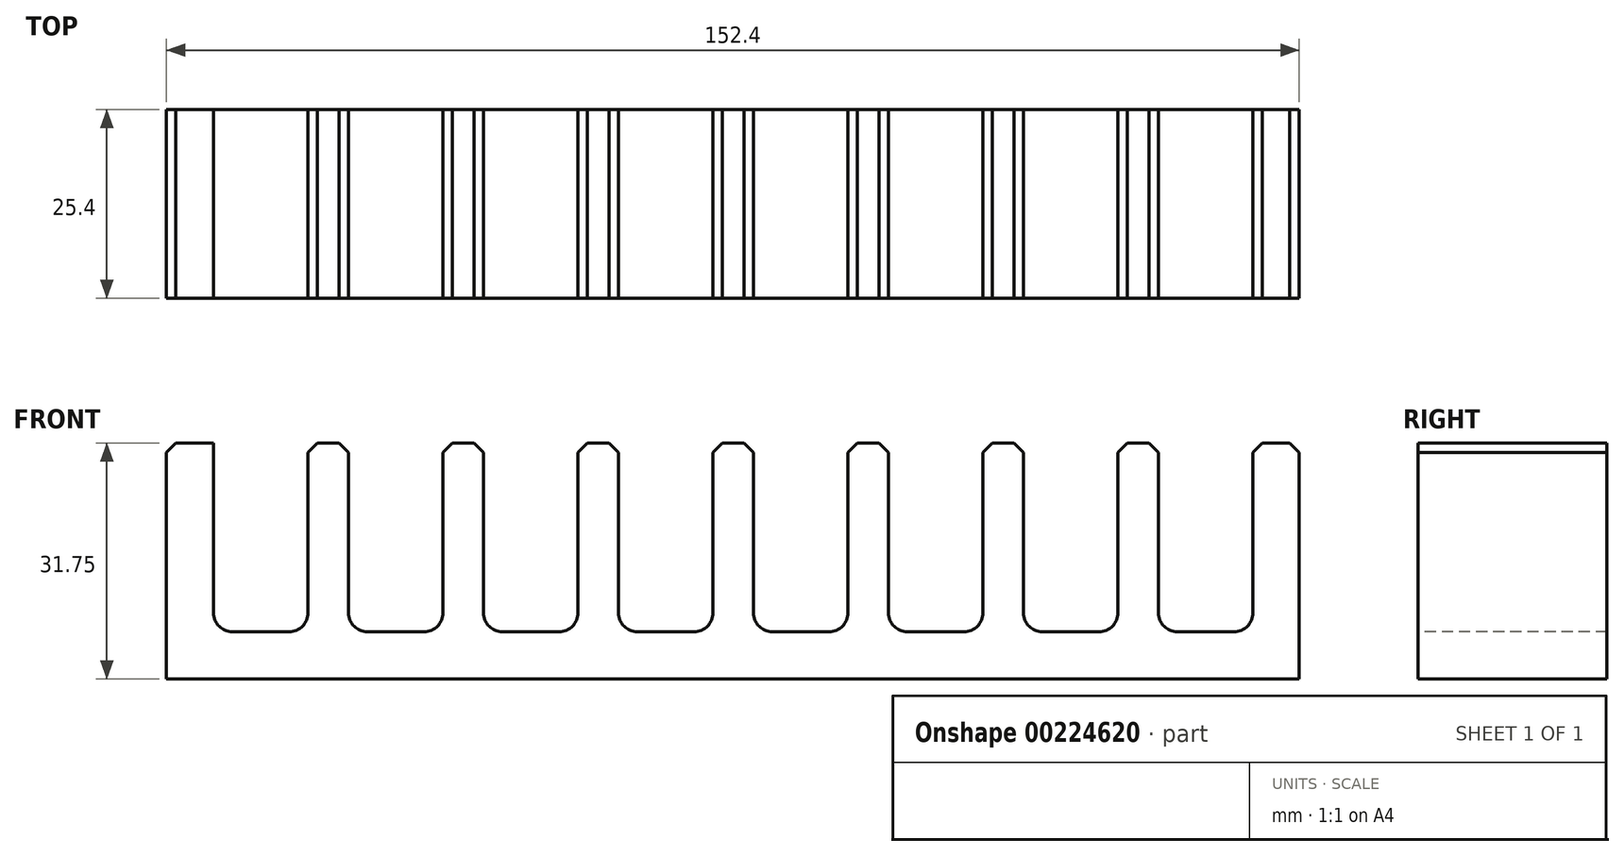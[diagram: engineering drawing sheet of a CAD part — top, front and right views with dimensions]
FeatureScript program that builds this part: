
annotation { "Feature Type Name" : "Feature", "Feature Type Description" : "" }
export const myFeature = defineFeature(function(context is Context, id is Id, definition is map)
    precondition{}
    {
        {
            var Q0;
            Q0=qCreatedBy(makeId("Top.planeOp"),FACE);
            var sketch = newSketch(context, id + "F0", { "sketchPlane" : qUnion([Q0])});
            skLineSegment(sketch, "E0.bottom", {"start": v(76.2, -12.7) * mm, "end": v(-76.2, -12.7) * mm});
            skLineSegment(sketch, "E0.top", {"start": v(76.2, 12.7) * mm, "end": v(-76.2, 12.7) * mm});
            skLineSegment(sketch, "E0.left", {"start": v(76.2, -12.7) * mm, "end": v(76.2, 12.7) * mm});
            skLineSegment(sketch, "E0.right", {"start": v(-76.2, -12.7) * mm, "end": v(-76.2, 12.7) * mm});
            skPoint(sketch, "E0.middle", {"position": v(0, 0) * mm});
            skSolve(sketch);
        }
        {
            var Q0;
            Q0 = qSketchRegion(id + "F0", true);
            extrude(context, id + "F1", {"entities" : qUnion([Q0]), "depth" : 31.75 * mm});
        }
        {
            var Q0;
            Q0=makeQuery(id+"F1.opExtrude","SWEPT_FACE",FACE,{"disambiguationData":[OSD([sQuery(id+"F0.wireOp",EDGE,"E0.bottom")])]});
            var sketch = newSketch(context, id + "F2", { "sketchPlane" : qUnion([Q0])});
            skLineSegment(sketch, "E1.bottom", {"start": v(-69.85, 31.75) * mm, "end": v(-57.15, 31.75) * mm});
            skLineSegment(sketch, "E1.top", {"start": v(-69.85, 6.35) * mm, "end": v(-57.15, 6.35) * mm});
            skLineSegment(sketch, "E1.left", {"start": v(-69.85, 31.75) * mm, "end": v(-69.85, 6.35) * mm});
            skLineSegment(sketch, "E1.right", {"start": v(-57.15, 31.75) * mm, "end": v(-57.15, 6.35) * mm});
            skLineSegment(sketch, "E2.1.0.0", {"start": v(-51.69, 31.75) * mm, "end": v(-38.99, 31.75) * mm});
            skLineSegment(sketch, "E2.1.0.1", {"start": v(-51.69, 6.35) * mm, "end": v(-38.99, 6.35) * mm});
            skLineSegment(sketch, "E2.1.0.2", {"start": v(-51.69, 31.75) * mm, "end": v(-51.69, 6.35) * mm});
            skLineSegment(sketch, "E2.1.0.3", {"start": v(-38.99, 31.75) * mm, "end": v(-38.99, 6.35) * mm});
            skLineSegment(sketch, "E2.2.0.0", {"start": v(-33.53, 31.75) * mm, "end": v(-20.83, 31.75) * mm});
            skLineSegment(sketch, "E2.2.0.1", {"start": v(-33.53, 6.35) * mm, "end": v(-20.83, 6.35) * mm});
            skLineSegment(sketch, "E2.2.0.2", {"start": v(-33.53, 31.75) * mm, "end": v(-33.53, 6.35) * mm});
            skLineSegment(sketch, "E2.2.0.3", {"start": v(-20.83, 31.75) * mm, "end": v(-20.83, 6.35) * mm});
            skLineSegment(sketch, "E2.3.0.0", {"start": v(-15.37, 31.75) * mm, "end": v(-2.67, 31.75) * mm});
            skLineSegment(sketch, "E2.3.0.1", {"start": v(-15.37, 6.35) * mm, "end": v(-2.67, 6.35) * mm});
            skLineSegment(sketch, "E2.3.0.2", {"start": v(-15.37, 31.75) * mm, "end": v(-15.37, 6.35) * mm});
            skLineSegment(sketch, "E2.3.0.3", {"start": v(-2.67, 31.75) * mm, "end": v(-2.67, 6.35) * mm});
            skLineSegment(sketch, "E2.4.0.0", {"start": v(2.8, 31.75) * mm, "end": v(15.5, 31.75) * mm});
            skLineSegment(sketch, "E2.4.0.1", {"start": v(2.8, 6.35) * mm, "end": v(15.5, 6.35) * mm});
            skLineSegment(sketch, "E2.4.0.2", {"start": v(2.8, 31.75) * mm, "end": v(2.8, 6.35) * mm});
            skLineSegment(sketch, "E2.4.0.3", {"start": v(15.5, 31.75) * mm, "end": v(15.5, 6.35) * mm});
            skLineSegment(sketch, "E2.5.0.0", {"start": v(20.95, 31.75) * mm, "end": v(33.65, 31.75) * mm});
            skLineSegment(sketch, "E2.5.0.1", {"start": v(20.95, 6.35) * mm, "end": v(33.65, 6.35) * mm});
            skLineSegment(sketch, "E2.5.0.2", {"start": v(20.95, 31.75) * mm, "end": v(20.95, 6.35) * mm});
            skLineSegment(sketch, "E2.5.0.3", {"start": v(33.65, 31.75) * mm, "end": v(33.65, 6.35) * mm});
            skLineSegment(sketch, "E2.6.0.0", {"start": v(39.12, 31.75) * mm, "end": v(51.82, 31.75) * mm});
            skLineSegment(sketch, "E2.6.0.1", {"start": v(39.12, 6.35) * mm, "end": v(51.82, 6.35) * mm});
            skLineSegment(sketch, "E2.6.0.2", {"start": v(39.12, 31.75) * mm, "end": v(39.12, 6.35) * mm});
            skLineSegment(sketch, "E2.6.0.3", {"start": v(51.82, 31.75) * mm, "end": v(51.82, 6.35) * mm});
            skLineSegment(sketch, "E2.7.0.0", {"start": v(57.28, 31.75) * mm, "end": v(69.98, 31.75) * mm});
            skLineSegment(sketch, "E2.7.0.1", {"start": v(57.28, 6.35) * mm, "end": v(69.98, 6.35) * mm});
            skLineSegment(sketch, "E2.7.0.2", {"start": v(57.28, 31.75) * mm, "end": v(57.28, 6.35) * mm});
            skLineSegment(sketch, "E2.7.0.3", {"start": v(69.98, 31.75) * mm, "end": v(69.98, 6.35) * mm});
            skLineSegment(sketch, "E2.direction1", {"start": v(-69.85, 6.35) * mm, "end": v(-51.69, 6.35) * mm, "construction": true});
            skSolve(sketch);
        }
        {
            var Q0;
            Q0 = qSketchRegion(id + "F2", true);
            extrude(context, id + "F3", {"entities" : qUnion([Q0]), "operationType" : NewBodyOperationType.REMOVE, "endBound" : BoundingType.THROUGH_ALL, "oppositeDirection" : true, "depth" : 25.4 * mm});
        }
        {
            var Q0;
            Q0=makeQuery(id+"F3.boolean.opBoolean","COPY",EDGE,{"derivedFrom":makeQuery(id+"F3.opExtrude","SWEPT_EDGE",EDGE,{"disambiguationData":[OSD([sQuery(id+"F2.wireOp",EDGE,"E1.top"),sQuery(id+"F2.wireOp",EDGE,"E1.left")])]})});
            var Q1;
            Q1=makeQuery(id+"F3.boolean.opBoolean","COPY",EDGE,{"derivedFrom":makeQuery(id+"F3.opExtrude","SWEPT_EDGE",EDGE,{"disambiguationData":[OSD([sQuery(id+"F2.wireOp",EDGE,"E1.top"),sQuery(id+"F2.wireOp",EDGE,"E1.right")])]})});
            var Q2;
            Q2=makeQuery(id+"F3.boolean.opBoolean","COPY",EDGE,{"derivedFrom":makeQuery(id+"F3.opExtrude","SWEPT_EDGE",EDGE,{"disambiguationData":[OSD([sQuery(id+"F2.wireOp",EDGE,"E2.1.0.1"),sQuery(id+"F2.wireOp",EDGE,"E2.1.0.3")])]})});
            var Q3;
            Q3=makeQuery(id+"F3.boolean.opBoolean","COPY",EDGE,{"derivedFrom":makeQuery(id+"F3.opExtrude","SWEPT_EDGE",EDGE,{"disambiguationData":[OSD([sQuery(id+"F2.wireOp",EDGE,"E2.2.0.1"),sQuery(id+"F2.wireOp",EDGE,"E2.2.0.3")])]})});
            var Q4;
            Q4=makeQuery(id+"F3.boolean.opBoolean","COPY",EDGE,{"derivedFrom":makeQuery(id+"F3.opExtrude","SWEPT_EDGE",EDGE,{"disambiguationData":[OSD([sQuery(id+"F2.wireOp",EDGE,"E2.3.0.1"),sQuery(id+"F2.wireOp",EDGE,"E2.3.0.3")])]})});
            var Q5;
            Q5=makeQuery(id+"F3.boolean.opBoolean","COPY",EDGE,{"derivedFrom":makeQuery(id+"F3.opExtrude","SWEPT_EDGE",EDGE,{"disambiguationData":[OSD([sQuery(id+"F2.wireOp",EDGE,"E2.4.0.1"),sQuery(id+"F2.wireOp",EDGE,"E2.4.0.3")])]})});
            var Q6;
            Q6=makeQuery(id+"F3.boolean.opBoolean","COPY",EDGE,{"derivedFrom":makeQuery(id+"F3.opExtrude","SWEPT_EDGE",EDGE,{"disambiguationData":[OSD([sQuery(id+"F2.wireOp",EDGE,"E2.5.0.1"),sQuery(id+"F2.wireOp",EDGE,"E2.5.0.3")])]})});
            var Q7;
            Q7=makeQuery(id+"F3.boolean.opBoolean","COPY",EDGE,{"derivedFrom":makeQuery(id+"F3.opExtrude","SWEPT_EDGE",EDGE,{"disambiguationData":[OSD([sQuery(id+"F2.wireOp",EDGE,"E2.6.0.1"),sQuery(id+"F2.wireOp",EDGE,"E2.6.0.3")])]})});
            var Q8;
            Q8=makeQuery(id+"F3.boolean.opBoolean","COPY",EDGE,{"derivedFrom":makeQuery(id+"F3.opExtrude","SWEPT_EDGE",EDGE,{"disambiguationData":[OSD([sQuery(id+"F2.wireOp",EDGE,"E2.7.0.1"),sQuery(id+"F2.wireOp",EDGE,"E2.7.0.3")])]})});
            var Q9;
            Q9=makeQuery(id+"F3.boolean.opBoolean","COPY",EDGE,{"derivedFrom":makeQuery(id+"F3.opExtrude","SWEPT_EDGE",EDGE,{"disambiguationData":[OSD([sQuery(id+"F2.wireOp",EDGE,"E2.7.0.1"),sQuery(id+"F2.wireOp",EDGE,"E2.7.0.2")])]})});
            var Q10;
            Q10=makeQuery(id+"F3.boolean.opBoolean","COPY",EDGE,{"derivedFrom":makeQuery(id+"F3.opExtrude","SWEPT_EDGE",EDGE,{"disambiguationData":[OSD([sQuery(id+"F2.wireOp",EDGE,"E2.6.0.1"),sQuery(id+"F2.wireOp",EDGE,"E2.6.0.2")])]})});
            var Q11;
            Q11=makeQuery(id+"F3.boolean.opBoolean","COPY",EDGE,{"derivedFrom":makeQuery(id+"F3.opExtrude","SWEPT_EDGE",EDGE,{"disambiguationData":[OSD([sQuery(id+"F2.wireOp",EDGE,"E2.5.0.1"),sQuery(id+"F2.wireOp",EDGE,"E2.5.0.2")])]})});
            var Q12;
            Q12=makeQuery(id+"F3.boolean.opBoolean","COPY",EDGE,{"derivedFrom":makeQuery(id+"F3.opExtrude","SWEPT_EDGE",EDGE,{"disambiguationData":[OSD([sQuery(id+"F2.wireOp",EDGE,"E2.4.0.1"),sQuery(id+"F2.wireOp",EDGE,"E2.4.0.2")])]})});
            var Q13;
            Q13=makeQuery(id+"F3.boolean.opBoolean","COPY",EDGE,{"derivedFrom":makeQuery(id+"F3.opExtrude","SWEPT_EDGE",EDGE,{"disambiguationData":[OSD([sQuery(id+"F2.wireOp",EDGE,"E2.3.0.1"),sQuery(id+"F2.wireOp",EDGE,"E2.3.0.2")])]})});
            var Q14;
            Q14=makeQuery(id+"F3.boolean.opBoolean","COPY",EDGE,{"derivedFrom":makeQuery(id+"F3.opExtrude","SWEPT_EDGE",EDGE,{"disambiguationData":[OSD([sQuery(id+"F2.wireOp",EDGE,"E2.2.0.1"),sQuery(id+"F2.wireOp",EDGE,"E2.2.0.2")])]})});
            var Q15;
            Q15=makeQuery(id+"F3.boolean.opBoolean","COPY",EDGE,{"derivedFrom":makeQuery(id+"F3.opExtrude","SWEPT_EDGE",EDGE,{"disambiguationData":[OSD([sQuery(id+"F2.wireOp",EDGE,"E2.1.0.1"),sQuery(id+"F2.wireOp",EDGE,"E2.1.0.2")])]})});
            fillet(context, id + "F4", {"entities" : qUnion([Q0, Q1, Q2, Q3, Q4, Q5, Q6, Q7, Q8, Q9, Q10, Q11, Q12, Q13, Q14, Q15]), "radius" : 2.54 * mm, "tangentPropagation" : true, "allowEdgeOverflow" : false});
        }
        {
            var Q0;
            Q0=makeQuery(id+"F3.boolean.opBoolean","COPY",EDGE,{"derivedFrom":makeQuery(id+"F3.opExtrude","SWEPT_EDGE",EDGE,{"disambiguationData":[OSD([sQuery(id+"F0.wireOp",EDGE,"E0.bottom"),sQuery(id+"F2.wireOp",EDGE,"E1.bottom"),sQuery(id+"F2.wireOp",EDGE,"E1.left")])]})});
            var Q1;
            Q1=makeQuery(id+"F1.opExtrude","CAP_EDGE",EDGE,{"disambiguationData":[OSD([sQuery(id+"F0.wireOp",EDGE,"E0.right")])],"isStart":false});
            var Q2;
            Q2=makeQuery(id+"F3.boolean.opBoolean","COPY",EDGE,{"derivedFrom":makeQuery(id+"F3.opExtrude","SWEPT_EDGE",EDGE,{"disambiguationData":[OSD([sQuery(id+"F0.wireOp",EDGE,"E0.bottom"),sQuery(id+"F2.wireOp",EDGE,"E1.bottom"),sQuery(id+"F2.wireOp",EDGE,"E1.right")])]})});
            var Q3;
            Q3=makeQuery(id+"F3.boolean.opBoolean","COPY",EDGE,{"derivedFrom":makeQuery(id+"F3.opExtrude","SWEPT_EDGE",EDGE,{"disambiguationData":[OSD([sQuery(id+"F0.wireOp",EDGE,"E0.bottom"),sQuery(id+"F2.wireOp",EDGE,"E2.1.0.0"),sQuery(id+"F2.wireOp",EDGE,"E2.1.0.2")])]})});
            var Q4;
            Q4=makeQuery(id+"F3.boolean.opBoolean","COPY",EDGE,{"derivedFrom":makeQuery(id+"F3.opExtrude","SWEPT_EDGE",EDGE,{"disambiguationData":[OSD([sQuery(id+"F0.wireOp",EDGE,"E0.bottom"),sQuery(id+"F2.wireOp",EDGE,"E2.1.0.0"),sQuery(id+"F2.wireOp",EDGE,"E2.1.0.3")])]})});
            var Q5;
            Q5=makeQuery(id+"F3.boolean.opBoolean","COPY",EDGE,{"derivedFrom":makeQuery(id+"F3.opExtrude","SWEPT_EDGE",EDGE,{"disambiguationData":[OSD([sQuery(id+"F0.wireOp",EDGE,"E0.bottom"),sQuery(id+"F2.wireOp",EDGE,"E2.2.0.0"),sQuery(id+"F2.wireOp",EDGE,"E2.2.0.2")])]})});
            var Q6;
            Q6=makeQuery(id+"F3.boolean.opBoolean","COPY",EDGE,{"derivedFrom":makeQuery(id+"F3.opExtrude","SWEPT_EDGE",EDGE,{"disambiguationData":[OSD([sQuery(id+"F0.wireOp",EDGE,"E0.bottom"),sQuery(id+"F2.wireOp",EDGE,"E2.2.0.0"),sQuery(id+"F2.wireOp",EDGE,"E2.2.0.3")])]})});
            var Q7;
            Q7=makeQuery(id+"F3.boolean.opBoolean","COPY",EDGE,{"derivedFrom":makeQuery(id+"F3.opExtrude","SWEPT_EDGE",EDGE,{"disambiguationData":[OSD([sQuery(id+"F0.wireOp",EDGE,"E0.bottom"),sQuery(id+"F2.wireOp",EDGE,"E2.3.0.0"),sQuery(id+"F2.wireOp",EDGE,"E2.3.0.2")])]})});
            var Q8;
            Q8=makeQuery(id+"F3.boolean.opBoolean","COPY",EDGE,{"derivedFrom":makeQuery(id+"F3.opExtrude","SWEPT_EDGE",EDGE,{"disambiguationData":[OSD([sQuery(id+"F0.wireOp",EDGE,"E0.bottom"),sQuery(id+"F2.wireOp",EDGE,"E2.3.0.0"),sQuery(id+"F2.wireOp",EDGE,"E2.3.0.3")])]})});
            var Q9;
            Q9=makeQuery(id+"F3.boolean.opBoolean","COPY",EDGE,{"derivedFrom":makeQuery(id+"F3.opExtrude","SWEPT_EDGE",EDGE,{"disambiguationData":[OSD([sQuery(id+"F0.wireOp",EDGE,"E0.bottom"),sQuery(id+"F2.wireOp",EDGE,"E2.4.0.0"),sQuery(id+"F2.wireOp",EDGE,"E2.4.0.2")])]})});
            var Q10;
            Q10=makeQuery(id+"F3.boolean.opBoolean","COPY",EDGE,{"derivedFrom":makeQuery(id+"F3.opExtrude","SWEPT_EDGE",EDGE,{"disambiguationData":[OSD([sQuery(id+"F0.wireOp",EDGE,"E0.bottom"),sQuery(id+"F2.wireOp",EDGE,"E2.4.0.0"),sQuery(id+"F2.wireOp",EDGE,"E2.4.0.3")])]})});
            var Q11;
            Q11=makeQuery(id+"F3.boolean.opBoolean","COPY",EDGE,{"derivedFrom":makeQuery(id+"F3.opExtrude","SWEPT_EDGE",EDGE,{"disambiguationData":[OSD([sQuery(id+"F0.wireOp",EDGE,"E0.bottom"),sQuery(id+"F2.wireOp",EDGE,"E2.5.0.0"),sQuery(id+"F2.wireOp",EDGE,"E2.5.0.2")])]})});
            var Q12;
            Q12=makeQuery(id+"F3.boolean.opBoolean","COPY",EDGE,{"derivedFrom":makeQuery(id+"F3.opExtrude","SWEPT_EDGE",EDGE,{"disambiguationData":[OSD([sQuery(id+"F0.wireOp",EDGE,"E0.bottom"),sQuery(id+"F2.wireOp",EDGE,"E2.5.0.0"),sQuery(id+"F2.wireOp",EDGE,"E2.5.0.3")])]})});
            var Q13;
            Q13=makeQuery(id+"F3.boolean.opBoolean","COPY",EDGE,{"derivedFrom":makeQuery(id+"F3.opExtrude","SWEPT_EDGE",EDGE,{"disambiguationData":[OSD([sQuery(id+"F0.wireOp",EDGE,"E0.bottom"),sQuery(id+"F2.wireOp",EDGE,"E2.6.0.0"),sQuery(id+"F2.wireOp",EDGE,"E2.6.0.2")])]})});
            var Q14;
            Q14=makeQuery(id+"F3.boolean.opBoolean","COPY",EDGE,{"derivedFrom":makeQuery(id+"F3.opExtrude","SWEPT_EDGE",EDGE,{"disambiguationData":[OSD([sQuery(id+"F0.wireOp",EDGE,"E0.bottom"),sQuery(id+"F2.wireOp",EDGE,"E2.6.0.0"),sQuery(id+"F2.wireOp",EDGE,"E2.6.0.3")])]})});
            var Q15;
            Q15=makeQuery(id+"F3.boolean.opBoolean","COPY",EDGE,{"derivedFrom":makeQuery(id+"F3.opExtrude","SWEPT_EDGE",EDGE,{"disambiguationData":[OSD([sQuery(id+"F0.wireOp",EDGE,"E0.bottom"),sQuery(id+"F2.wireOp",EDGE,"E2.7.0.0"),sQuery(id+"F2.wireOp",EDGE,"E2.7.0.2")])]})});
            var Q16;
            Q16=makeQuery(id+"F3.boolean.opBoolean","COPY",EDGE,{"derivedFrom":makeQuery(id+"F3.opExtrude","SWEPT_EDGE",EDGE,{"disambiguationData":[OSD([sQuery(id+"F0.wireOp",EDGE,"E0.bottom"),sQuery(id+"F2.wireOp",EDGE,"E2.7.0.0"),sQuery(id+"F2.wireOp",EDGE,"E2.7.0.3")])]})});
            var Q17;
            Q17=makeQuery(id+"F1.opExtrude","CAP_EDGE",EDGE,{"disambiguationData":[OSD([sQuery(id+"F0.wireOp",EDGE,"E0.left")])],"isStart":false});
            chamfer(context, id + "F5", {"entities" : qUnion([Q0, Q1, Q2, Q3, Q4, Q5, Q6, Q7, Q8, Q9, Q10, Q11, Q12, Q13, Q14, Q15, Q16, Q17]), "width" : 1.27 * mm, "tangentPropagation" : true});
        }
    });
